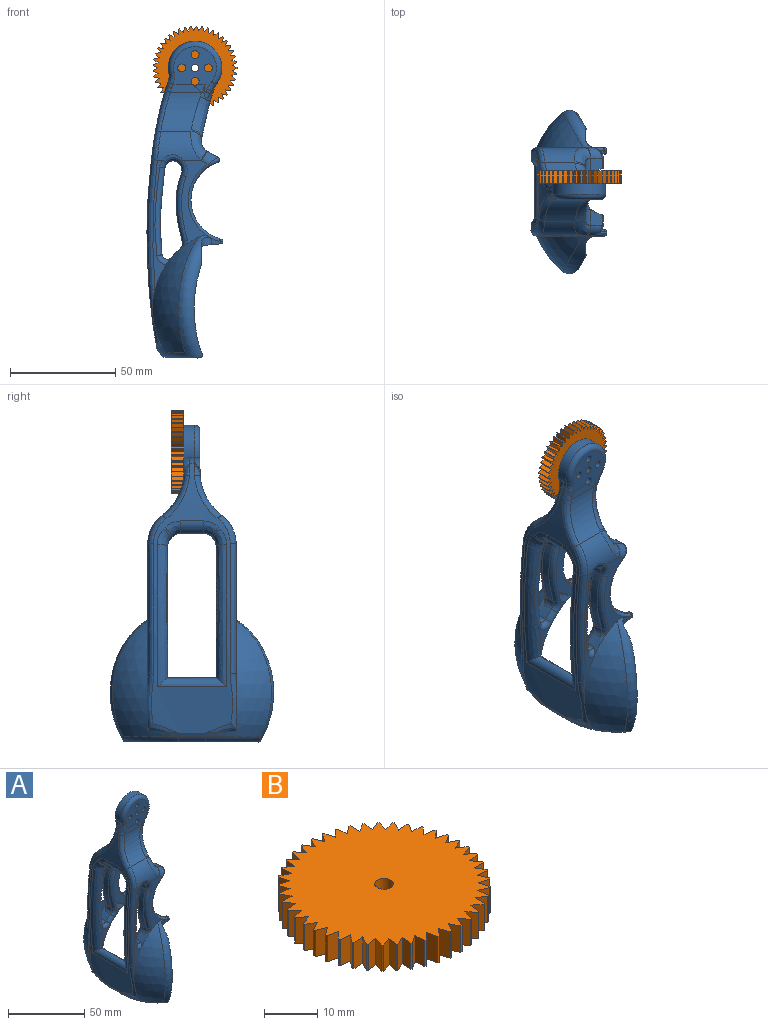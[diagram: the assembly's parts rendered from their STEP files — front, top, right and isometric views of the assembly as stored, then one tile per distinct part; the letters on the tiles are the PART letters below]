
ASSEMBLY  parts=2 mates=1
PART A: 219 faces, bbox 38.1x83.8x156.5 mm
  f0: plane 10.68x10.5mm, normal (1,0,0), area 27.9mm2, adj f1,f212,f213,f214
  f1: torus R=34.56mm, axis (-0.87,0.5,0), area 481mm2, adj f0,f2,f211,f212,f214,f215
  f2: torus R=29.73mm, axis (0,0,1), area 244.9mm2, adj f1,f3,f214,f215
  f3: cylinder r=5.08mm len=12.7mm, axis (0,-1,0), area 106mm2, adj f2,f4,f209,f210
  f4: cylinder r=34.92mm len=29.42mm, axis (0,1,0), area 398.8mm2, adj f3,f5,f208,f214
  f5: plane 23.03x0.66mm, normal (0,0,1), area 7.6mm2, adj f4,f6,f206,f207,f208,f214
  f6: bspline ~79.74x7.85mm, area 412mm2, adj f5,f7,f201,f202,f203,f204,f205,f206
  f7: extruded ~127.7x38.85mm, area 1315.1mm2, adj f6,f8,f181,f182,f183,f184,f185,f186
  f8: bspline ~8.9x5.37mm, area 0.7mm2, adj f7,f9,f194
  f9: bspline ~5.74x5.43mm, area 1.6mm2, adj f8,f10,f179,f180,f181,f194
  f10: bspline ~3.48x2.21mm, area 3.6mm2, adj f9,f11,f179,f194
  f11: cylinder r=50.8mm len=16.38mm, axis (1,0,0), area 58.7mm2, adj f10,f12,f175,f176,f177,f178,f194
  f12: cylinder r=25.4mm len=19.49mm, axis (1,0,0), area 319.2mm2, adj f11,f13,f172,f173,f174,f193
  f13: cylinder r=17.18mm len=20.7mm, axis (1,0,0), area 240.4mm2, adj f12,f14,f169,f170,f171,f192,f211
  f14: plane 61.28x6.25mm, normal (0,-1,0), area 97mm2, adj f13,f15,f167,f168,f191,f215
  f15: torus R=6.35mm, axis (0,-1,0), area 10.9mm2, adj f14,f16,f167,f171
  f16: cylinder r=3.81mm len=6.36mm, axis (0,-1,0), area 38.7mm2, adj f15,f17,f18,f165,f166,f171,f204
  f17: bspline ~3.49x3.24mm, area 1.4mm2, adj f16,f18,f204,f205
  f18: bspline ~10.77x3.7mm, area 25.5mm2, adj f16,f17,f19,f32
  f19: bspline ~4.44x3.76mm, area 4.6mm2, adj f18,f20,f32,f165
  f20: torus R=7.62mm, axis (0,-1,0), area 22.8mm2, adj f19,f21,f165,f201
  f21: bspline ~36.28x5.93mm, area 126.1mm2, adj f20,f22,f31,f201
  f22: extruded ~31.61x4.45mm, area 143mm2, adj f21,f23,f29,f165
  f23: cylinder r=3.81mm len=4.45mm, axis (0,-1,0), area 19mm2, adj f22,f24,f28,f31
  f24: cylinder r=37.24mm len=10.33mm, axis (0,-1,0), area 50.2mm2, adj f23,f25,f27,f28,f168,f215
  f25: cylinder r=2.54mm len=4.45mm, axis (0,-1,0), area 26.1mm2, adj f24,f26,f166,f168,f202
  f26: torus R=5.08mm, axis (0,-1,0), area 26.4mm2, adj f25,f27,f201,f202
  f27: torus R=34.7mm, axis (0,-1,0), area 21.5mm2, adj f24,f26,f31,f201
  f28: torus R=6.35mm, axis (0,-1,0), area 12.2mm2, adj f23,f24,f29,f211
  f29: bspline ~36.28x5.92mm, area 126.1mm2, adj f22,f28,f30,f211
  f30: torus R=7.62mm, axis (0,-1,0), area 26.1mm2, adj f29,f165,f170,f211
  f31: torus R=6.35mm, axis (0,-1,0), area 21.1mm2, adj f21,f23,f27,f201
  f32: cylinder r=5.08mm len=26.82mm, axis (-1,0,0), area 86.3mm2, adj f18,f19,f33,f163,f164,f201,f205
  f33: plane 7.72x5.51mm, normal (0.49,0,0.87), area 36.8mm2, adj f32,f34,f141,f142,f163,f164
  f34: cylinder r=5.08mm len=7.55mm, axis (0,-1,0), area 38mm2, adj f33,f35,f36,f140,f169,f172
  f35: torus R=10.16mm, axis (0,-1,0), area 2mm2, adj f34,f142,f169,f211
  f36: bspline ~5.31x2.81mm, area 14.2mm2, adj f34,f37,f140,f141
  f37: cylinder r=5.08mm len=11.03mm, axis (0,-1,0), area 48.1mm2, adj f36,f38,f139,f140
  f38: plane 18.27x11.03mm, normal (0,0,-1), area 201.6mm2, adj f37,f39,f141,f198
  f39: cylinder r=5.08mm len=21.37mm, axis (1,0,0), area 78.2mm2, adj f38,f40,f138,f139,f197
  f40: plane 22.97x0.83mm, normal (0,-0.71,-0.71), area 26.2mm2, adj f39,f41,f138,f196
  f41: cylinder r=5.08mm len=26.82mm, axis (-1,0,0), area 86.3mm2, adj f40,f42,f135,f136,f137,f138,f195
  f42: plane 61.87x28.71mm, normal (0,-1,0), area 320mm2, adj f41,f43,f44,f128,f129,f130,f131,f132
  f43: cylinder r=40mm len=9.53mm, axis (-0.89,0,-0.46), area 3.8mm2, adj f42,f217,f218
  f44: cylinder r=1.27mm len=3.81mm, axis (0,-1,0), area 11mm2, adj f42,f45,f128,f134
  f45: bspline ~6.51x4.5mm, area 16.2mm2, adj f44,f46,f124,f134
  f46: sphere r=1.27mm, area 2.2mm2, adj f45,f47,f123
  f47: cylinder r=1.27mm len=1.23mm, axis (0,1,0), area 1.1mm2, adj f46,f48,f122,f134
  f48: sphere r=1.27mm, area 1.3mm2, adj f47,f49,f113
  f49: torus R=20.32mm, axis (0,-1,0), area 90.2mm2, adj f48,f50,f134,f218
  f50: bspline ~7.92x6.39mm, area 19.9mm2, adj f49,f51,f134,f135
  f51: cylinder r=5.08mm len=7.84mm, axis (0.87,0,-0.49), area 38.5mm2, adj f50,f52,f138,f218
  f52: torus R=10.16mm, axis (0,-1,0), area 2mm2, adj f51,f53,f112,f218
  f53: cylinder r=5.08mm len=7.55mm, axis (0,-1,0), area 38mm2, adj f52,f54,f112,f138,f139,f140
  f54: bspline ~7.5x7.23mm, area 7.9mm2, adj f53,f55,f90,f112
  f55: bspline ~24.1x17.42mm, area 165mm2, adj f54,f56,f61,f84,f85,f90,f140,f173
  f56: bspline ~6.18x5.81mm, area 4.6mm2, adj f55,f57,f85,f90
  f57: bspline ~5.62x5.33mm, area 1.4mm2, adj f56,f58,f59,f85
  f58: bspline ~6.46x6.44mm, area 1.4mm2, adj f57,f59,f85
  f59: cylinder r=50.8mm len=16.64mm, axis (1,0,0), area 60.8mm2, adj f57,f58,f60,f85,f90,f178,f183
  f60: bspline ~9.57x8.31mm, area 15.5mm2, adj f59,f85,f180,f181,f182,f183
  f61: bspline ~6.18x5.81mm, area 7.7mm2, adj f55,f62,f82,f83
  f62: bspline ~6.11x5.76mm, area 7.7mm2, adj f61,f63,f81,f173
  f63: bspline ~5.7x5.53mm, area 1.6mm2, adj f62,f64,f78,f80
  f64: bspline ~4.11x4.03mm, area 1.4mm2, adj f63,f65,f77,f81
  f65: bspline ~4.67x4.61mm, area 5.3mm2, adj f64,f66,f75,f76
  f66: bspline ~2.76x2.53mm, area 1.9mm2, adj f65,f67,f69,f74,f180
  f67: bspline ~3.21x2.98mm, area 1.4mm2, adj f66,f68,f75,f177
  f68: torus R=10.16mm, axis (0,1,0), area 189.3mm2, adj f67,f177,f179,f180
  f69: bspline ~6.18x5.59mm, area 0mm2, adj f66,f70,f76
  f70: bspline ~6.18x5.59mm, area 0mm2, adj f69,f71,f74
  f71: bspline ~7.14x6.82mm, area 2.6mm2, adj f70,f72,f76,f82
  f72: bspline ~4.72x4.66mm, area 9.4mm2, adj f71,f73,f74,f85,f180
  f73: bspline ~4.11x4.03mm, area 3.8mm2, adj f72,f82,f83,f85
  f74: bspline ~3.07x2.86mm, area 1.9mm2, adj f66,f70,f72,f180
  f75: bspline ~5x4.5mm, area 12.9mm2, adj f65,f67,f77,f177
  f76: bspline ~7.37x6.9mm, area 2.6mm2, adj f65,f69,f71,f81
  f77: bspline ~3.14x2.95mm, area 4mm2, adj f64,f75,f78,f177
  f78: bspline ~4.68x3.37mm, area 5.8mm2, adj f63,f77,f79,f174,f177
  f79: bspline ~1.88x1.59mm, area 0.1mm2, adj f78,f80,f173,f174
  f80: bspline ~4.71x4.45mm, area 0mm2, adj f63,f79,f173
  f81: bspline ~5.76x5.41mm, area 2.4mm2, adj f62,f64,f76,f82
  f82: bspline ~5.76x5.41mm, area 2.4mm2, adj f61,f71,f73,f81
  f83: bspline ~5.35x5.21mm, area 5.7mm2, adj f61,f73,f84,f85
  f84: bspline ~6.11x5.64mm, area 1.4mm2, adj f55,f83,f85
  f85: plane 29.98x26.37mm, normal (0,1,0), area 402.4mm2, adj f55,f56,f57,f58,f59,f60,f72,f73
  f86: cylinder r=1.75mm len=7.62mm, axis (0,-1,0), area 83.9mm2, adj f85,f177
  f87: cylinder r=1.91mm len=7.62mm, axis (0,-1,0), area 91.2mm2, adj f85,f177
  f88: cylinder r=1.91mm len=7.62mm, axis (0,-1,0), area 91.2mm2, adj f85,f177
  f89: cylinder r=1.91mm len=7.62mm, axis (0,-1,0), area 91.2mm2, adj f85,f177
  f90: cylinder r=25.4mm len=19.49mm, axis (1,0,0), area 319.2mm2, adj f54,f55,f56,f59,f91,f184
  f91: cylinder r=17.18mm len=20.7mm, axis (1,0,0), area 240.4mm2, adj f90,f92,f110,f111,f112,f185,f218
  f92: plane 61.28x6.25mm, normal (0,1,0), area 97mm2, adj f91,f93,f108,f109,f186,f217
  f93: torus R=6.35mm, axis (0,-1,0), area 10.9mm2, adj f92,f94,f109,f110
  f94: cylinder r=3.81mm len=6.36mm, axis (0,-1,0), area 38.7mm2, adj f93,f95,f105,f106,f107,f110,f136
  f95: cylinder r=5.08mm len=5.52mm, axis (0,-1,0), area 26.9mm2, adj f94,f96,f104,f111,f133,f137
  f96: torus R=7.62mm, axis (0,-1,0), area 26.1mm2, adj f95,f97,f111,f218
  f97: bspline ~36.28x5.93mm, area 126.1mm2, adj f96,f98,f104,f218
  f98: torus R=6.35mm, axis (0,-1,0), area 12.2mm2, adj f97,f99,f100,f218
  f99: cylinder r=3.81mm len=4.45mm, axis (0,-1,0), area 19mm2, adj f98,f100,f104,f131
  f100: cylinder r=37.24mm len=10.33mm, axis (0,-1,0), area 50.2mm2, adj f98,f99,f101,f108,f130,f217
  f101: cylinder r=2.54mm len=4.45mm, axis (0,-1,0), area 26.1mm2, adj f100,f102,f107,f108,f129
  f102: bspline ~3.88x3.23mm, area 6.4mm2, adj f101,f103,f129,f207
  f103: bspline ~44.9x6.38mm, area 216mm2, adj f102,f106,f107,f207
  f104: extruded ~31.61x4.45mm, area 143mm2, adj f95,f97,f99,f132
  f105: bspline ~3.49x3.24mm, area 1.4mm2, adj f94,f106,f136,f195
  f106: bspline ~4.15x3.54mm, area 9.3mm2, adj f94,f103,f105,f207
  f107: extruded ~41.3x4.38mm, area 180.1mm2, adj f94,f101,f103,f109
  f108: torus R=5.08mm, axis (0,-1,0), area 24.2mm2, adj f92,f100,f101,f109
  f109: bspline ~49.48x5.47mm, area 166.3mm2, adj f92,f93,f107,f108
  f110: bspline ~10.47x5.06mm, area 32.7mm2, adj f91,f93,f94,f111
  f111: bspline ~4.33x4.05mm, area 2.5mm2, adj f91,f95,f96,f110
  f112: bspline ~15.31x11.18mm, area 93.8mm2, adj f52,f53,f54,f91
  f113: cylinder r=1.27mm len=1.27mm, axis (0,0,1), area 2mm2, adj f48,f114,f122,f218
  f114: extruded ~9.27x5.26mm, area 31.5mm2, adj f113,f115,f116,f117,f118,f121,f122,f124
  f115: cylinder r=1.27mm len=1.27mm, axis (0,0,-1), area 1.6mm2, adj f114,f116,f122,f123
  f116: plane 5.34x1.35mm, normal (0,-1,0), area 2.5mm2, adj f114,f115,f124
  f117: cylinder r=31.91mm len=3.05mm, axis (-1,0,0), area 1mm2, adj f114,f118,f124,f208
  f118: cylinder r=1.27mm len=8.28mm, axis (0,1,0), area 9.3mm2, adj f114,f117,f119,f121
  f119: plane 10.68x10.5mm, normal (1,0,0), area 27.9mm2, adj f118,f120,f121,f208
  f120: torus R=34.56mm, axis (-0.87,-0.5,0), area 481mm2, adj f119,f121,f208,f209,f217,f218
  f121: cylinder r=5.08mm len=5.39mm, axis (0,0,-1), area 25.7mm2, adj f114,f118,f119,f120,f218
  f122: plane 0.97x0.64mm, normal (1,0,0), area 0.6mm2, adj f47,f113,f114,f115,f123
  f123: bspline ~1.74x1.38mm, area 0.3mm2, adj f46,f115,f122,f124
  f124: torus R=32.01mm, axis (0,-1,0), area 19mm2, adj f45,f114,f116,f117,f123,f125,f128,f208
  f125: bspline ~2.78x2.22mm, area 3.5mm2, adj f124,f126,f127,f208
  f126: cylinder r=1.27mm len=3.81mm, axis (0,-1,0), area 3.5mm2, adj f125,f127,f128,f208
  f127: plane 0.82x0.26mm, normal (1,0,0), area 0mm2, adj f125,f126,f208
  f128: cylinder r=34.55mm len=3.81mm, axis (0,-1,0), area 12.4mm2, adj f42,f44,f124,f126
  f129: torus R=5.08mm, axis (0,-1,0), area 26.4mm2, adj f42,f101,f102,f130
  f130: torus R=34.7mm, axis (0,-1,0), area 21.5mm2, adj f42,f100,f129,f131
  f131: torus R=6.35mm, axis (0,-1,0), area 21.1mm2, adj f42,f99,f130,f132
  f132: bspline ~36.28x5.92mm, area 126.1mm2, adj f42,f104,f131,f133
  f133: torus R=7.62mm, axis (0,-1,0), area 22.8mm2, adj f42,f95,f132,f137
  f134: cylinder r=19.05mm len=36.38mm, axis (0,1,0), area 357.2mm2, adj f42,f44,f45,f47,f49,f50,f135
  f135: cylinder r=1.27mm len=4.88mm, axis (0,1,0), area 13.4mm2, adj f41,f42,f50,f134,f138
  f136: bspline ~10.88x3.7mm, area 25.5mm2, adj f41,f94,f105,f137
  f137: bspline ~3.74x3.27mm, area 4.6mm2, adj f41,f95,f133,f136
  f138: plane 7.72x5.51mm, normal (0.49,0,0.87), area 36.8mm2, adj f39,f40,f41,f51,f53,f135
  f139: bspline ~5.55x4.19mm, area 14.2mm2, adj f37,f39,f53,f140
  f140: extruded ~20.13x15.16mm, area 123.5mm2, adj f34,f36,f37,f53,f55,f139,f173
  f141: cylinder r=5.08mm len=21.37mm, axis (1,0,0), area 78.2mm2, adj f33,f36,f38,f164,f199
  f142: cylinder r=5.08mm len=7.84mm, axis (-0.87,0,0.49), area 38.5mm2, adj f33,f35,f143,f211
  f143: bspline ~7.92x6.39mm, area 19.9mm2, adj f142,f144,f162,f163
  f144: cylinder r=19.05mm len=36.38mm, axis (0,1,0), area 357.2mm2, adj f143,f145,f160,f161,f162,f163,f201
  f145: cylinder r=1.27mm len=1.23mm, axis (0,1,0), area 1.1mm2, adj f144,f146,f158,f159
  f146: sphere r=1.27mm, area 2.2mm2, adj f145,f147,f160
  f147: bspline ~1.74x1.38mm, area 0.3mm2, adj f146,f148,f153,f158
  f148: cylinder r=1.27mm len=1.27mm, axis (0,0,-1), area 1.6mm2, adj f147,f149,f150,f158
  f149: plane 5.34x1.35mm, normal (0,1,0), area 2.5mm2, adj f148,f150,f153
  f150: extruded ~10.29x5.32mm, area 32.6mm2, adj f148,f149,f151,f152,f153,f158,f211,f212
  f151: plane 0.78x0.31mm, normal (-1,0,0), area 0.1mm2, adj f150,f153,f214
  f152: cylinder r=1.27mm len=1.27mm, axis (0,0,-1), area 2mm2, adj f150,f158,f159,f211
  f153: torus R=32.01mm, axis (0,1,0), area 19.1mm2, adj f147,f149,f150,f151,f154,f157,f160,f214
  f154: cylinder r=34.55mm len=3.81mm, axis (0,1,0), area 12.4mm2, adj f153,f155,f161,f201
  f155: cylinder r=1.27mm len=3.81mm, axis (0,1,0), area 3.5mm2, adj f154,f156,f157,f214
  f156: plane 0.82x0.26mm, normal (1,0,0), area 0mm2, adj f155,f157,f214
  f157: bspline ~2.78x2.22mm, area 3.5mm2, adj f153,f155,f156,f214
  f158: plane 0.97x0.64mm, normal (1,0,0), area 0.6mm2, adj f145,f147,f148,f150,f152
  f159: sphere r=1.27mm, area 2.1mm2, adj f145,f152,f162
  f160: bspline ~7.52x4.5mm, area 16.2mm2, adj f144,f146,f153,f161
  f161: cylinder r=1.27mm len=3.81mm, axis (0,1,0), area 11mm2, adj f144,f154,f160,f201
  f162: torus R=20.32mm, axis (0,-1,0), area 90.2mm2, adj f143,f144,f159,f211
  f163: cylinder r=1.27mm len=4.88mm, axis (0,1,0), area 13.4mm2, adj f32,f33,f143,f144,f201
  f164: plane 22.97x0.83mm, normal (0,0.71,-0.71), area 26.2mm2, adj f32,f33,f141,f200
  f165: cylinder r=5.08mm len=5.52mm, axis (0,-1,0), area 26.9mm2, adj f16,f19,f20,f22,f30,f170
  f166: extruded ~41.3x4.38mm, area 180.1mm2, adj f16,f25,f167,f203
  f167: bspline ~49.48x5.46mm, area 166.3mm2, adj f14,f15,f166,f168
  f168: torus R=5.08mm, axis (0,-1,0), area 24.2mm2, adj f14,f24,f25,f167
  f169: bspline ~14.85x10.66mm, area 93.8mm2, adj f13,f34,f35,f172
  f170: bspline ~4.05x3.77mm, area 2.5mm2, adj f13,f30,f165,f171
  f171: bspline ~10.79x5.06mm, area 32.7mm2, adj f13,f15,f16,f170
  f172: bspline ~7.5x7.23mm, area 7.9mm2, adj f12,f34,f169,f173
  f173: bspline ~23.15x16.23mm, area 166mm2, adj f12,f55,f62,f79,f80,f140,f172,f174
  f174: bspline ~6.11x5.76mm, area 5mm2, adj f12,f78,f79,f173,f175,f177
  f175: bspline ~5.76x5.41mm, area 1.4mm2, adj f11,f174,f176,f177
  f176: bspline ~7.37x6.9mm, area 1.4mm2, adj f11,f175,f177
  f177: plane 22.66x20.66mm, normal (0,-1,0), area 259.4mm2, adj f11,f67,f68,f75,f77,f78,f86,f87
  f178: cylinder r=1.91mm len=7.62mm, axis (0,-1,0), area 91.2mm2, adj f11,f59,f85,f177
  f179: bspline ~6.61x2.93mm, area 17mm2, adj f9,f10,f68,f177
  f180: cylinder r=12.7mm len=25.4mm, axis (0,1,0), area 262.1mm2, adj f9,f60,f66,f68,f72,f74,f85,f181
  f181: cylinder r=5.08mm len=2.87mm, axis (0,-1,0), area 5.9mm2, adj f7,f9,f60,f180
  f182: bspline ~8.9x5.37mm, area 0.7mm2, adj f7,f60,f183
  f183: bspline ~10.99x6mm, area 12.3mm2, adj f7,f59,f60,f182,f184
  f184: bspline ~25.76x15.33mm, area 95.9mm2, adj f7,f90,f183,f185
  f185: bspline ~15.42x9.9mm, area 63.7mm2, adj f7,f91,f184,f186
  f186: bspline ~78.66x5.71mm, area 270.9mm2, adj f7,f92,f185,f187
  f187: bspline ~31.5x7.94mm, area 65mm2, adj f7,f186,f188,f217
  f188: bspline ~15.61x5.4mm, area 24mm2, adj f7,f187,f217
  f189: bspline ~16.68x5.75mm, area 22.2mm2, adj f7,f190,f215
  f190: bspline ~28.92x6.66mm, area 65mm2, adj f7,f189,f191,f215
  f191: bspline ~78.66x5.71mm, area 270.9mm2, adj f7,f14,f190,f192
  f192: bspline ~15.42x9.9mm, area 63.7mm2, adj f7,f13,f191,f193
  f193: bspline ~24.47x13.55mm, area 95.9mm2, adj f7,f12,f192,f194
  f194: bspline ~10.99x6mm, area 14.4mm2, adj f7,f8,f9,f10,f11,f193
  f195: bspline ~10.51x7.44mm, area 45.6mm2, adj f7,f41,f105,f196,f207
  f196: bspline ~9.95x9.58mm, area 10.2mm2, adj f7,f40,f195,f197
  f197: bspline ~9.09x7.82mm, area 46.4mm2, adj f7,f39,f196,f198
  f198: cylinder r=5.08mm len=11.03mm, axis (0,-1,0), area 97.1mm2, adj f7,f38,f197,f199
  f199: bspline ~9.09x7.82mm, area 46.5mm2, adj f7,f141,f198,f200
  f200: bspline ~9.95x9.58mm, area 10.2mm2, adj f7,f164,f199,f205
  f201: plane 61.87x28.71mm, normal (0,1,0), area 320mm2, adj f6,f20,f21,f26,f27,f31,f32,f144
  f202: bspline ~3.88x3.23mm, area 6.4mm2, adj f6,f25,f26,f203
  f203: bspline ~45.74x6.38mm, area 216mm2, adj f6,f166,f202,f204
  f204: bspline ~4.15x3.54mm, area 9.3mm2, adj f6,f16,f17,f203
  f205: bspline ~10.08x7.86mm, area 45.7mm2, adj f6,f7,f17,f32,f200
  f206: cylinder r=3.81mm len=33.02mm, axis (0,-1,0), area 178.8mm2, adj f5,f6,f7,f207
  f207: bspline ~79.74x7.85mm, area 412mm2, adj f5,f7,f42,f102,f103,f106,f195,f206
  f208: sphere r=34.92mm, area 1738.1mm2, adj f4,f5,f42,f117,f119,f120,f124,f125
  f209: torus R=29.73mm, axis (0,0,1), area 244.9mm2, adj f3,f120,f208,f217
  f210: cylinder r=40mm len=12.7mm, axis (0,1,0), area 26.8mm2, adj f3,f7,f215,f217
  f211: plane 40.09x18.4mm, normal (0,-1,0), area 203.4mm2, adj f1,f13,f28,f29,f30,f35,f142,f150
  f212: cylinder r=5.08mm len=5.39mm, axis (0,0,1), area 25.7mm2, adj f0,f1,f150,f211,f213
  f213: cylinder r=1.27mm len=7.11mm, axis (0,-1,0), area 8.3mm2, adj f0,f150,f212,f214
  f214: sphere r=34.92mm, area 1738.8mm2, adj f0,f1,f2,f4,f5,f6,f150,f151
  f215: sphere r=40mm, area 1032.4mm2, adj f1,f2,f14,f24,f189,f190,f201,f210
  f216: cylinder r=40mm len=9.53mm, axis (-0.89,0,-0.46), area 3.8mm2, adj f201,f211,f215
  f217: sphere r=40mm, area 1032.4mm2, adj f42,f43,f92,f100,f120,f187,f188,f209
  f218: plane 40.09x18.42mm, normal (0,1,0), area 203.4mm2, adj f43,f49,f51,f52,f91,f96,f97,f98
PART B: 138 faces, bbox 39.8x39.8x6 mm
  f0: plane 6.04x0.34mm, normal (-1,-0.07,0), area 2mm2, adj f1,f134,f135,f136
  f1: plane 6.04x2.3mm, normal (-0.37,-0.93,0), area 15mm2, adj f0,f2,f135,f136
  f2: plane 6.04x1.96mm, normal (-0.61,0.79,0), area 15mm2, adj f1,f3,f135,f136
  f3: plane 6.04x0.33mm, normal (-0.98,-0.21,0), area 2mm2, adj f2,f4,f135,f136
  f4: plane 6.04x2.41mm, normal (-0.23,-0.97,0), area 15mm2, adj f3,f5,f135,f136
  f5: plane 6.04x1.77mm, normal (-0.71,0.7,0), area 15mm2, adj f4,f6,f135,f136
  f6: plane 6.04x0.32mm, normal (-0.94,-0.34,0), area 2mm2, adj f5,f7,f135,f136
  f7: plane 6.04x2.47mm, normal (-0.1,-1,0), area 15mm2, adj f6,f8,f135,f136
  f8: plane 6.04x1.99mm, normal (-0.8,0.59,0), area 15mm2, adj f7,f9,f135,f136
  f9: plane 6.04x0.3mm, normal (-0.88,-0.47,0), area 2mm2, adj f8,f10,f135,f136
  f10: plane 6.04x2.47mm, normal (0.04,-1,0), area 15mm2, adj f9,f11,f135,f136
  f11: plane 6.04x2.18mm, normal (-0.88,0.48,0), area 15mm2, adj f10,f12,f135,f136
  f12: plane 6.04x0.27mm, normal (-0.81,-0.59,0), area 2mm2, adj f11,f13,f135,f136
  f13: plane 6.04x2.44mm, normal (0.18,-0.98,0), area 15mm2, adj f12,f14,f135,f136
  f14: plane 6.04x2.32mm, normal (-0.94,0.35,0), area 15mm2, adj f13,f15,f135,f136
  f15: plane 6.04x0.24mm, normal (-0.72,-0.69,0), area 2mm2, adj f14,f16,f135,f136
  f16: plane 6.04x2.35mm, normal (0.32,-0.95,0), area 15mm2, adj f15,f17,f135,f136
  f17: plane 6.04x2.42mm, normal (-0.98,0.22,0), area 15mm2, adj f16,f18,f135,f136
  f18: plane 6.04x0.27mm, normal (-0.62,-0.79,0), area 2mm2, adj f17,f19,f135,f136
  f19: plane 6.04x2.22mm, normal (0.45,-0.9,0), area 15mm2, adj f18,f20,f135,f136
  f20: plane 6.04x2.47mm, normal (-1,0.08,0), area 15mm2, adj f19,f21,f135,f136
  f21: plane 6.04x0.29mm, normal (-0.5,-0.87,0), area 2mm2, adj f20,f22,f135,f136
  f22: plane 6.04x2.04mm, normal (0.57,-0.82,0), area 15mm2, adj f21,f23,f135,f136
  f23: plane 6.04x2.47mm, normal (-1,-0.06,0), area 15mm2, adj f22,f24,f135,f136
  f24: plane 6.04x0.31mm, normal (-0.37,-0.93,0), area 2mm2, adj f23,f25,f135,f136
  f25: plane 6.04x1.83mm, normal (0.67,-0.74,0), area 15mm2, adj f24,f26,f135,f136
  f26: plane 6.04x2.43mm, normal (-0.98,-0.2,0), area 15mm2, adj f25,f27,f135,f136
  f27: plane 6.04x0.33mm, normal (-0.24,-0.97,0), area 2mm2, adj f26,f28,f135,f136
  f28: plane 6.04x1.91mm, normal (0.77,-0.64,0), area 15mm2, adj f27,f29,f135,f136
  f29: plane 6.04x2.33mm, normal (-0.94,-0.33,0), area 15mm2, adj f28,f30,f135,f136
  f30: plane 6.04x0.34mm, normal (-0.1,-0.99,0), area 2mm2, adj f29,f31,f135,f136
  f31: plane 6.04x2.11mm, normal (0.85,-0.52,0), area 15mm2, adj f30,f32,f135,f136
  f32: plane 6.04x2.2mm, normal (-0.89,-0.46,0), area 15mm2, adj f31,f33,f135,f136
  f33: plane 6.04x0.34mm, normal (0.03,-1,0), area 2mm2, adj f32,f34,f135,f136
  f34: plane 6.04x2.27mm, normal (0.92,-0.4,0), area 15mm2, adj f33,f35,f135,f136
  f35: plane 6.04x2.01mm, normal (-0.81,-0.58,0), area 15mm2, adj f34,f36,f135,f136
  f36: plane 6.04x0.33mm, normal (0.17,-0.98,0), area 2mm2, adj f35,f37,f135,f136
  f37: plane 6.04x2.39mm, normal (0.96,-0.27,0), area 15mm2, adj f36,f38,f135,f136
  f38: plane 6.04x1.79mm, normal (-0.72,-0.69,0), area 15mm2, adj f37,f39,f135,f136
  f39: plane 6.04x0.32mm, normal (0.31,-0.95,0), area 2mm2, adj f38,f40,f135,f136
  f40: plane 6.04x2.46mm, normal (0.99,-0.13,0), area 15mm2, adj f39,f41,f135,f136
  f41: plane 6.04x1.94mm, normal (-0.62,-0.78,0), area 15mm2, adj f40,f42,f135,f136
  f42: plane 6.04x0.3mm, normal (0.44,-0.9,0), area 2mm2, adj f41,f43,f135,f136
  f43: plane 6.04x2.48mm, normal (1,0.01,0), area 15mm2, adj f42,f44,f135,f136
  f44: plane 6.04x2.14mm, normal (-0.51,-0.86,0), area 15mm2, adj f43,f45,f135,f136
  f45: plane 6.04x0.28mm, normal (0.56,-0.83,0), area 2mm2, adj f44,f46,f135,f136
  f46: plane 6.04x2.45mm, normal (0.99,0.15,0), area 15mm2, adj f45,f47,f135,f136
  f47: plane 6.04x2.29mm, normal (-0.38,-0.92,0), area 15mm2, adj f46,f48,f135,f136
  f48: plane 6.04x0.25mm, normal (0.67,-0.74,0), area 2mm2, adj f47,f49,f135,f136
  f49: plane 6.04x2.38mm, normal (0.96,0.28,0), area 15mm2, adj f48,f50,f135,f136
  f50: plane 6.04x2.4mm, normal (-0.25,-0.97,0), area 15mm2, adj f49,f51,f135,f136
  f51: plane 6.04x0.26mm, normal (0.77,-0.64,0), area 2mm2, adj f50,f52,f135,f136
  f52: plane 6.04x2.25mm, normal (0.91,0.41,0), area 15mm2, adj f51,f53,f135,f136
  f53: plane 6.04x2.46mm, normal (-0.11,-0.99,0), area 15mm2, adj f52,f54,f135,f136
  f54: plane 6.04x0.29mm, normal (0.85,-0.53,0), area 2mm2, adj f53,f55,f135,f136
  f55: plane 6.04x2.09mm, normal (0.84,0.54,0), area 15mm2, adj f54,f56,f135,f136
  f56: plane 6.04x2.48mm, normal (0.03,-1,0), area 15mm2, adj f55,f57,f135,f136
  f57: plane 6.04x0.31mm, normal (0.91,-0.41,0), area 2mm2, adj f56,f58,f135,f136
  f58: plane 6.04x1.88mm, normal (0.76,0.65,0), area 15mm2, adj f57,f59,f135,f136
  f59: plane 6.04x2.44mm, normal (0.17,-0.99,0), area 15mm2, adj f58,f60,f135,f136
  f60: plane 6.04x0.32mm, normal (0.96,-0.28,0), area 2mm2, adj f59,f61,f135,f136
  f61: plane 6.04x1.85mm, normal (0.66,0.75,0), area 15mm2, adj f60,f62,f135,f136
  f62: plane 6.04x2.36mm, normal (0.3,-0.95,0), area 15mm2, adj f61,f63,f135,f136
  f63: plane 6.04x0.33mm, normal (0.99,-0.14,0), area 2mm2, adj f62,f64,f135,f136
  f64: plane 6.04x2.06mm, normal (0.55,0.83,0), area 15mm2, adj f63,f65,f135,f136
  f65: plane 6.04x2.23mm, normal (0.43,-0.9,0), area 15mm2, adj f64,f66,f135,f136
  f66: plane 6.04x0.34mm, normal (1,0,0), area 2mm2, adj f65,f67,f135,f136
  f67: plane 6.04x2.23mm, normal (0.43,0.9,0), area 15mm2, adj f66,f68,f135,f136
  f68: plane 6.04x2.06mm, normal (0.55,-0.83,0), area 15mm2, adj f67,f69,f135,f136
  f69: plane 6.04x0.33mm, normal (0.99,0.14,0), area 2mm2, adj f68,f70,f135,f136
  f70: plane 6.04x2.36mm, normal (0.3,0.95,0), area 15mm2, adj f69,f71,f135,f136
  f71: plane 6.04x1.85mm, normal (0.66,-0.75,0), area 15mm2, adj f70,f72,f135,f136
  f72: plane 6.04x0.32mm, normal (0.96,0.28,0), area 2mm2, adj f71,f73,f135,f136
  f73: plane 6.04x2.44mm, normal (0.17,0.99,0), area 15mm2, adj f72,f74,f135,f136
  f74: plane 6.04x1.88mm, normal (0.76,-0.65,0), area 15mm2, adj f73,f75,f135,f136
  f75: plane 6.04x0.31mm, normal (0.91,0.41,0), area 2mm2, adj f74,f76,f135,f136
  f76: plane 6.04x2.48mm, normal (0.03,1,0), area 15mm2, adj f75,f77,f135,f136
  f77: plane 6.04x2.09mm, normal (0.84,-0.54,0), area 15mm2, adj f76,f78,f135,f136
  f78: plane 6.04x0.29mm, normal (0.85,0.53,0), area 2mm2, adj f77,f79,f135,f136
  f79: plane 6.04x2.46mm, normal (-0.11,0.99,0), area 15mm2, adj f78,f80,f135,f136
  f80: plane 6.04x2.25mm, normal (0.91,-0.41,0), area 15mm2, adj f79,f81,f135,f136
  f81: plane 6.04x0.26mm, normal (0.77,0.64,0), area 2mm2, adj f80,f82,f135,f136
  f82: plane 6.04x2.4mm, normal (-0.25,0.97,0), area 15mm2, adj f81,f83,f135,f136
  f83: plane 6.04x2.38mm, normal (0.96,-0.28,0), area 15mm2, adj f82,f84,f135,f136
  f84: plane 6.04x0.25mm, normal (0.67,0.74,0), area 2mm2, adj f83,f85,f135,f136
  f85: plane 6.04x2.29mm, normal (-0.38,0.92,0), area 15mm2, adj f84,f86,f135,f136
  f86: plane 6.04x2.45mm, normal (0.99,-0.15,0), area 15mm2, adj f85,f87,f135,f136
  f87: plane 6.04x0.28mm, normal (0.56,0.83,0), area 2mm2, adj f86,f88,f135,f136
  f88: plane 6.04x2.14mm, normal (-0.51,0.86,0), area 15mm2, adj f87,f89,f135,f136
  f89: plane 6.04x2.48mm, normal (1,-0.01,0), area 15mm2, adj f88,f90,f135,f136
  f90: plane 6.04x0.3mm, normal (0.44,0.9,0), area 2mm2, adj f89,f91,f135,f136
  f91: plane 6.04x1.94mm, normal (-0.62,0.78,0), area 15mm2, adj f90,f92,f135,f136
  f92: plane 6.04x2.46mm, normal (0.99,0.13,0), area 15mm2, adj f91,f93,f135,f136
  f93: plane 6.04x0.32mm, normal (0.31,0.95,0), area 2mm2, adj f92,f94,f135,f136
  f94: plane 6.04x1.79mm, normal (-0.72,0.69,0), area 15mm2, adj f93,f95,f135,f136
  f95: plane 6.04x2.39mm, normal (0.96,0.27,0), area 15mm2, adj f94,f96,f135,f136
  f96: plane 6.04x0.33mm, normal (0.17,0.98,0), area 2mm2, adj f95,f97,f135,f136
  f97: plane 6.04x2.01mm, normal (-0.81,0.58,0), area 15mm2, adj f96,f98,f135,f136
  f98: plane 6.04x2.27mm, normal (0.92,0.4,0), area 15mm2, adj f97,f99,f135,f136
  f99: plane 6.04x0.34mm, normal (0.03,1,0), area 2mm2, adj f98,f100,f135,f136
  f100: plane 6.04x2.2mm, normal (-0.89,0.46,0), area 15mm2, adj f99,f101,f135,f136
  f101: plane 6.04x2.11mm, normal (0.85,0.52,0), area 15mm2, adj f100,f102,f135,f136
  f102: plane 6.04x0.34mm, normal (-0.1,0.99,0), area 2mm2, adj f101,f103,f135,f136
  f103: plane 6.04x2.33mm, normal (-0.94,0.33,0), area 15mm2, adj f102,f104,f135,f136
  f104: plane 6.04x1.91mm, normal (0.77,0.64,0), area 15mm2, adj f103,f105,f135,f136
  f105: plane 6.04x0.33mm, normal (-0.24,0.97,0), area 2mm2, adj f104,f106,f135,f136
  f106: plane 6.04x2.43mm, normal (-0.98,0.2,0), area 15mm2, adj f105,f107,f135,f136
  f107: plane 6.04x1.83mm, normal (0.67,0.74,0), area 15mm2, adj f106,f108,f135,f136
  f108: plane 6.04x0.31mm, normal (-0.37,0.93,0), area 2mm2, adj f107,f109,f135,f136
  f109: plane 6.04x2.47mm, normal (-1,0.06,0), area 15mm2, adj f108,f110,f135,f136
  f110: plane 6.04x2.04mm, normal (0.57,0.82,0), area 15mm2, adj f109,f111,f135,f136
  f111: plane 6.04x0.29mm, normal (-0.5,0.87,0), area 2mm2, adj f110,f112,f135,f136
  f112: plane 6.04x2.47mm, normal (-1,-0.08,0), area 15mm2, adj f111,f113,f135,f136
  f113: plane 6.04x2.22mm, normal (0.45,0.9,0), area 15mm2, adj f112,f114,f135,f136
  f114: plane 6.04x0.27mm, normal (-0.62,0.79,0), area 2mm2, adj f113,f115,f135,f136
  f115: plane 6.04x2.42mm, normal (-0.98,-0.22,0), area 15mm2, adj f114,f116,f135,f136
  f116: plane 6.04x2.35mm, normal (0.32,0.95,0), area 15mm2, adj f115,f117,f135,f136
  f117: plane 6.04x0.24mm, normal (-0.72,0.69,0), area 2mm2, adj f116,f118,f135,f136
  f118: plane 6.04x2.32mm, normal (-0.94,-0.35,0), area 15mm2, adj f117,f119,f135,f136
  f119: plane 6.04x2.44mm, normal (0.18,0.98,0), area 15mm2, adj f118,f120,f135,f136
  f120: plane 6.04x0.27mm, normal (-0.81,0.59,0), area 2mm2, adj f119,f121,f135,f136
  f121: plane 6.04x2.18mm, normal (-0.88,-0.48,0), area 15mm2, adj f120,f122,f135,f136
  f122: plane 6.04x2.47mm, normal (0.04,1,0), area 15mm2, adj f121,f123,f135,f136
  f123: plane 6.04x0.3mm, normal (-0.88,0.47,0), area 2mm2, adj f122,f124,f135,f136
  f124: plane 6.04x1.99mm, normal (-0.8,-0.59,0), area 15mm2, adj f123,f125,f135,f136
  f125: plane 6.04x2.47mm, normal (-0.1,1,0), area 15mm2, adj f124,f126,f135,f136
  f126: plane 6.04x0.32mm, normal (-0.94,0.34,0), area 2mm2, adj f125,f127,f135,f136
  f127: plane 6.04x1.77mm, normal (-0.71,-0.7,0), area 15mm2, adj f126,f128,f135,f136
  f128: plane 6.04x2.41mm, normal (-0.23,0.97,0), area 15mm2, adj f127,f129,f135,f136
  f129: plane 6.04x0.33mm, normal (-0.98,0.21,0), area 2mm2, adj f128,f130,f135,f136
  f130: plane 6.04x1.96mm, normal (-0.61,-0.79,0), area 15mm2, adj f129,f131,f135,f136
  f131: plane 6.04x2.3mm, normal (-0.37,0.93,0), area 15mm2, adj f130,f132,f135,f136
  f132: plane 6.04x0.34mm, normal (-1,0.07,0), area 2mm2, adj f131,f133,f135,f136
  f133: plane 6.04x2.15mm, normal (-0.49,-0.87,0), area 15mm2, adj f132,f134,f135,f136
  f134: plane 6.04x2.15mm, normal (-0.49,0.87,0), area 15mm2, adj f0,f133,f135,f136
  f135: plane 39.83x39.81mm, normal (0,0,1), area 1116mm2, adj f0,f1,f2,f3,f4,f5,f6,f7
  f136: plane 39.83x39.81mm, normal (0,0,-1), area 1116mm2, adj f0,f1,f2,f3,f4,f5,f6,f7
  f137: cylinder r=1.75mm len=6.04mm, axis (0,0,1), area 66.5mm2, adj f135,f136
PLACE A t=(-51.78,-46.95,5.84)mm
PLACE B rot(axis=(1,0,0),90deg) t=(-68.87,-37.1,68.61)mm
MATE fastened B.f137 <-> A.f68  axis (0,-1,0) through (-68.87,-43.14,68.61)mm
